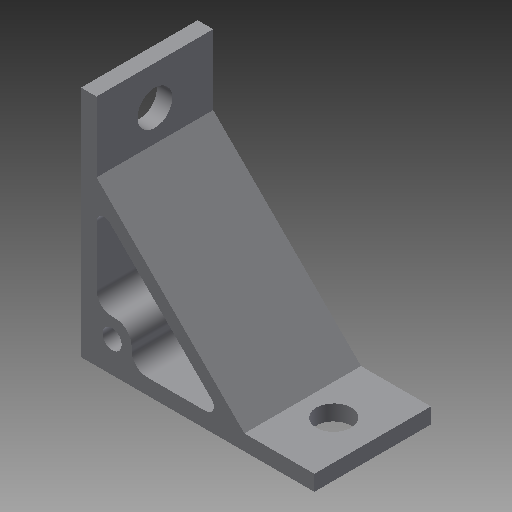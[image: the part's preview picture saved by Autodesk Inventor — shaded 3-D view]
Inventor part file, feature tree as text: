
AUTODESK INVENTOR PART (.ipt)
format: ipt  version: 2018 (Build 220112000, 112)  size: 137,216 bytes
history: native  units: mm
features: other x28, sketch x5, extrude x3, hole x2
ambient origin geometry x8: Origin, YZ Plane, XZ Plane, XY Plane, X Axis, Y Axis, Z Axis, Center Point
bodies: Solid1 (feature_tree)
feature tree (38):
  extrude  "Extrusion1"  Depth=30.0mm TaperAngle=0.0deg
  extrude  "Extrusion2"  [1 undecoded]
  extrude  "Extrusion3"  [1 undecoded]
  hole  "Drilling 2"  [1 undecoded]
  hole  "Drilling 3"  [1 undecoded]
  other  "cover_panel_hole_a_XY"
  other  "cover_panel_hole_a_YZ"
  other  "cover_panel_hole_a_ZX"
  other  "cover_panel_hole_a_X"
  other  "cover_panel_hole_a_Y"
  other  "cover_panel_hole_a_Z"
  other  "cover_panel_hole_a_Center"
  other  "cover_panel_hole_b_XY"
  other  "cover_panel_hole_b_YZ"
  other  "cover_panel_hole_b_ZX"
  other  "cover_panel_hole_b_X"
  other  "cover_panel_hole_b_Y"
  other  "cover_panel_hole_b_Z"
  other  "cover_panel_hole_b_Center"
  other  "side_1_XY"
  other  "side_1_YZ"
  other  "side_1_ZX"
  other  "side_1_X"
  other  "side_1_Y"
  other  "side_1_Z"
  other  "side_1_Center"
  other  "side_2_XY"
  other  "side_2_YZ"
  other  "side_2_ZX"
  other  "side_2_X"
  other  "side_2_Y"
  other  "side_2_Z"
  other  "side_2_Center"
  sketch  "Skizze_1"  dims[d0=30.0mm d1=0.0mm d2=32.0mm d3=0.0mm]
  sketch  "Skizze_2"  dims[d4=32.0mm d5=0.0mm]
  sketch  "Skizze_3"  dims[d6=9.0mm d7=6.0mm d8=4.0mm d9=2.0mm d10=90.0deg d11=5.0mm d12=0.0mm]
  sketch  "Sketch4"  dims[d13=9.0mm d14=6.0mm d15=4.0mm d16=2.0mm d17=90.0deg d18=5.0mm d19=0.0mm]
  sketch  "Sketch5"
note: 4 required parameter values undecoded (feature->parameter linkage not recoverable at this tier; creation-order binding heuristic only, values carry confidence <= 0.55)
